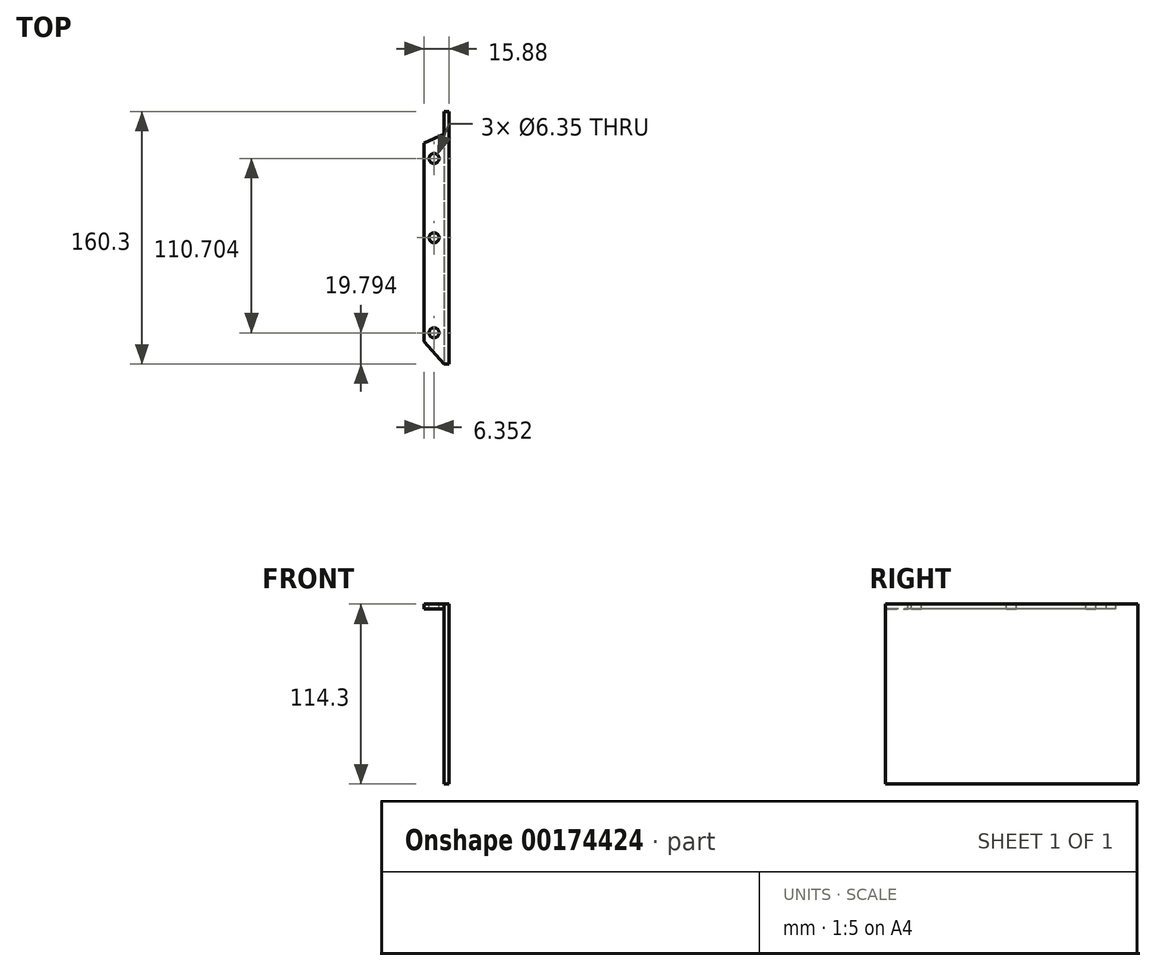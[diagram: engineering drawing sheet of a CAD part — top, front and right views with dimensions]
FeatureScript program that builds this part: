
annotation { "Feature Type Name" : "Feature", "Feature Type Description" : "" }
export const myFeature = defineFeature(function(context is Context, id is Id, definition is map)
    precondition{}
    {
        {
            var Q0;
            Q0=qCreatedBy(makeId("Top.planeOp"),FACE);
            var sketch = newSketch(context, id + "F0", { "sketchPlane" : qUnion([Q0])});
            skLineSegment(sketch, "E0.bottom", {"start": v(1.59, 80.15) * mm, "end": v(-1.59, 80.15) * mm});
            skLineSegment(sketch, "E0.top", {"start": v(1.59, -80.15) * mm, "end": v(-1.59, -80.15) * mm});
            skLineSegment(sketch, "E0.left", {"start": v(1.59, 80.15) * mm, "end": v(1.59, -80.15) * mm});
            skLineSegment(sketch, "E0.right", {"start": v(-1.59, 80.15) * mm, "end": v(-1.59, -80.15) * mm});
            skPoint(sketch, "E0.middle", {"position": v(0, 0) * mm});
            skLineSegment(sketch, "E1", {"start": v(-1.59, 80.15) * mm, "end": v(-1.59, 80.15) * mm});
            skLineSegment(sketch, "E2", {"start": v(-1.59, 80.15) * mm, "end": v(1.59, 80.15) * mm});
            skSolve(sketch);
        }
        {
            var Q0;
            Q0=qSketchRegion(id+"F0",true);
            extrude(context, id + "F1", {"entities" : qUnion([Q0]), "depth" : 114.3 * mm});
        }
        {
            var Q0;
            Q0=makeQuery(id+"F1.opExtrude","SWEPT_FACE",FACE,{"disambiguationData":[OSD([sQuery(id+"F0.wireOp",EDGE,"E0.right")])]});
            var sketch = newSketch(context, id + "F2", { "sketchPlane" : qUnion([Q0])});
            skPoint(sketch, "E3", {"position": v(-66, 114.3) * mm});
            skPoint(sketch, "E4", {"position": v(80.15, 114.3) * mm});
            skLineSegment(sketch, "E5.bottom", {"start": v(-66, 114.3) * mm, "end": v(80.15, 114.3) * mm});
            skLineSegment(sketch, "E5.top", {"start": v(-66, 111.13) * mm, "end": v(80.15, 111.13) * mm});
            skLineSegment(sketch, "E5.left", {"start": v(-66, 114.3) * mm, "end": v(-66, 111.13) * mm});
            skLineSegment(sketch, "E5.right", {"start": v(80.15, 114.3) * mm, "end": v(80.15, 111.13) * mm});
            skSolve(sketch);
        }
        {
            var Q0;
            Q0 = qSketchRegion(id + "F2", true);
            extrude(context, id + "F3", {"entities" : qUnion([Q0]), "operationType" : NewBodyOperationType.ADD, "depth" : 12.7 * mm, "offsetDistance" : 25.4 * mm});
        }
        {
            var Q0;
            Q0=makeQuery(id+"F3.boolean.opBoolean","MERGE",FACE,{"derivedFrom":[makeQuery(id+"F1.opExtrude","CAP_FACE",FACE,{"disambiguationData":[OSD([sQuery(id+"F0.wireOp",EDGE,"E0.top"),sQuery(id+"F0.wireOp",EDGE,"E0.left"),sQuery(id+"F0.wireOp",EDGE,"E0.right"),sQuery(id+"F0.wireOp",EDGE,"E2")])],"isStart":false}),makeQuery(id+"F3.opExtrude","SWEPT_FACE",FACE,{"disambiguationData":[OSD([sQuery(id+"F2.wireOp",EDGE,"E5.bottom")])]})]});
            var sketch = newSketch(context, id + "F4", { "sketchPlane" : qUnion([Q0])});
            skLineSegment(sketch, "E6", {"start": v(-1.59, 66) * mm, "end": v(-14.29, 60.1) * mm});
            skLineSegment(sketch, "E7", {"start": v(-14.29, 60.1) * mm, "end": v(-14.29, 66) * mm});
            skLineSegment(sketch, "E8", {"start": v(-14.29, 66) * mm, "end": v(-1.59, 66) * mm});
            skLineSegment(sketch, "E9", {"start": v(-1.59, -80.15) * mm, "end": v(-14.29, -65.96) * mm});
            skPoint(sketch, "E9.startSnap0", {"position": v(-1.59, 73.08) * mm});
            skLineSegment(sketch, "E10", {"start": v(-14.29, -65.96) * mm, "end": v(-14.29, -80.15) * mm});
            skLineSegment(sketch, "E11", {"start": v(-14.29, -80.15) * mm, "end": v(-1.59, -80.15) * mm});
            skSolve(sketch);
        }
        {
            var Q0;
            Q0 = qSketchRegion(id + "F4", true);
            extrude(context, id + "F5", {"entities" : qUnion([Q0]), "operationType" : NewBodyOperationType.REMOVE, "oppositeDirection" : true, "depth" : 25.4 * mm, "offsetDistance" : 25.4 * mm});
        }
        {
            var Q0;
            Q0=makeQuery(id+"F3.boolean.opBoolean","MERGE",FACE,{"derivedFrom":[makeQuery(id+"F1.opExtrude","CAP_FACE",FACE,{"disambiguationData":[OSD([sQuery(id+"F0.wireOp",EDGE,"E0.top"),sQuery(id+"F0.wireOp",EDGE,"E0.left"),sQuery(id+"F0.wireOp",EDGE,"E0.right"),sQuery(id+"F0.wireOp",EDGE,"E2")])],"isStart":false}),makeQuery(id+"F3.opExtrude","SWEPT_FACE",FACE,{"disambiguationData":[OSD([sQuery(id+"F2.wireOp",EDGE,"E5.bottom")])]})]});
            var sketch = newSketch(context, id + "F6", { "sketchPlane" : qUnion([Q0])});
            skLineSegment(sketch, "E12", {"start": v(-7.94, 63.05) * mm, "end": v(-7.94, -73.06) * mm});
            skCircle(sketch, "E13", {"center": v(-7.94, 0) * mm, "radius": 3.18 * mm});
            skCircle(sketch, "E14", {"center": v(-7.94, -60.36) * mm, "radius": 3.18 * mm});
            skCircle(sketch, "E15", {"center": v(-7.94, 50.35) * mm, "radius": 3.18 * mm});
            skSolve(sketch);
        }
        {
            var Q0;
            Q0 = qSketchRegion(id + "F6", true);
            extrude(context, id + "F7", {"entities" : qUnion([Q0]), "operationType" : NewBodyOperationType.REMOVE, "oppositeDirection" : true, "depth" : 25.4 * mm, "offsetDistance" : 25.4 * mm});
        }
    });
